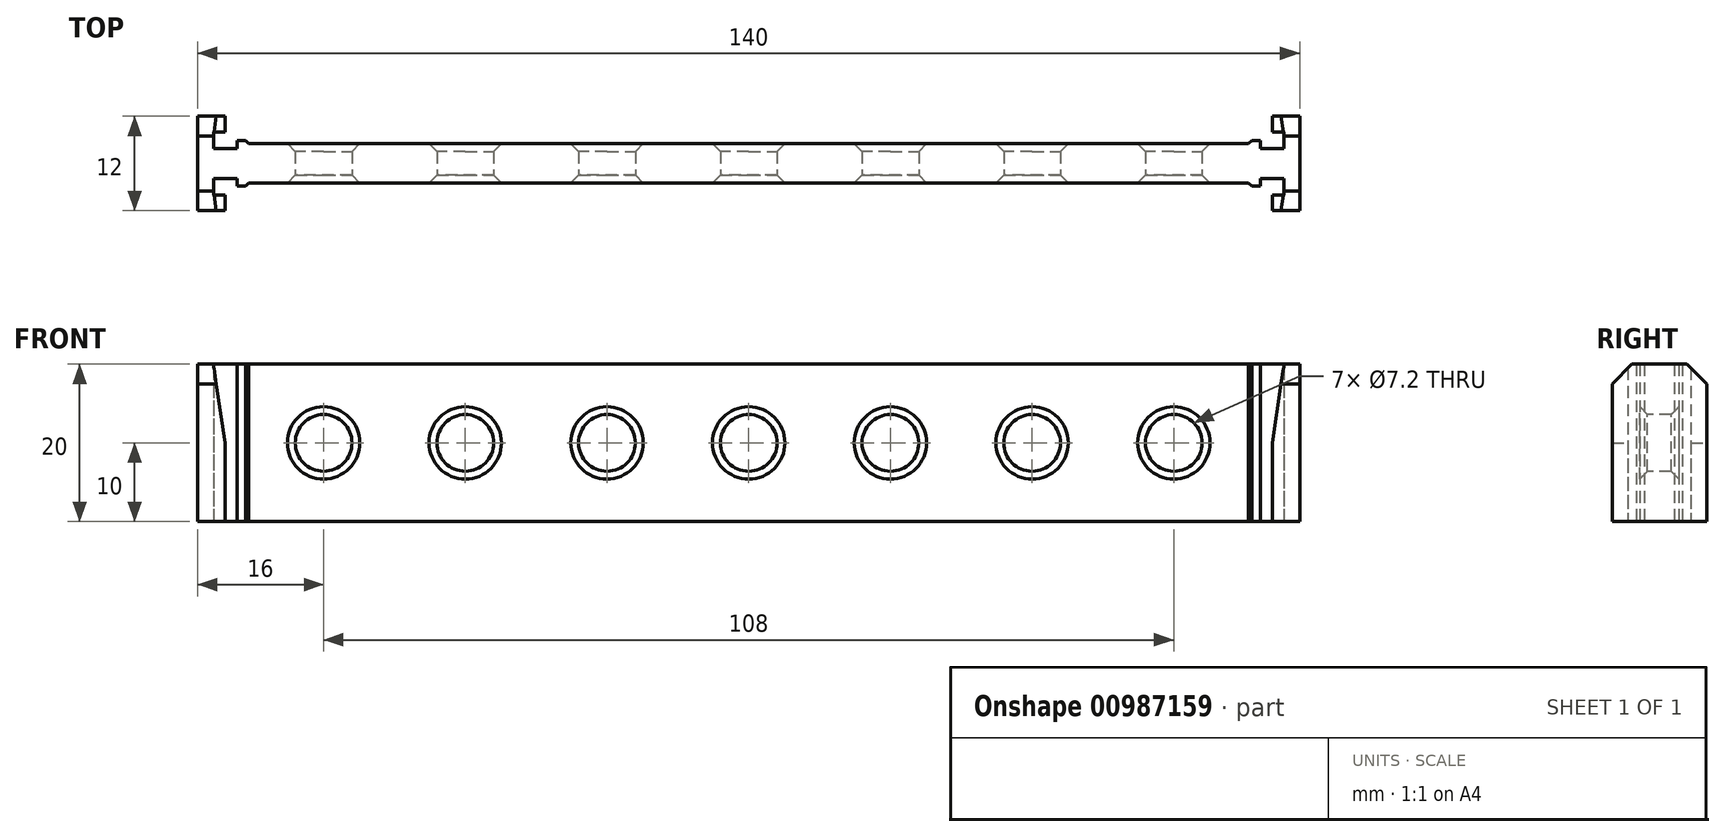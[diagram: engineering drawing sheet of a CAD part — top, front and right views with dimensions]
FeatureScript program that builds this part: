
annotation { "Feature Type Name" : "Feature", "Feature Type Description" : "" }
export const myFeature = defineFeature(function(context is Context, id is Id, definition is map)
    precondition{}
    {
        {
            var Q0;
            Q0=qCreatedBy(makeId("Top.planeOp"),FACE);
            var sketch = newSketch(context, id + "F0", { "sketchPlane" : qUnion([Q0])});
            skLineSegment(sketch, "E0", {"start": v(-70, 0) * mm, "end": v(-70, 6) * mm});
            skLineSegment(sketch, "E1", {"start": v(-70, 6) * mm, "end": v(-66.5, 6) * mm});
            skLineSegment(sketch, "E2", {"start": v(-66.5, 6) * mm, "end": v(-66.5, 4) * mm});
            skLineSegment(sketch, "E3", {"start": v(-66.5, 4) * mm, "end": v(-68, 4) * mm});
            skLineSegment(sketch, "E4", {"start": v(-68, 4) * mm, "end": v(-68, 1.9) * mm});
            skLineSegment(sketch, "E5", {"start": v(-68, 1.9) * mm, "end": v(-65, 1.9) * mm});
            skLineSegment(sketch, "E6", {"start": v(-65, 1.9) * mm, "end": v(-65, 2.9) * mm});
            skLineSegment(sketch, "E7", {"start": v(0, 2.5) * mm, "end": v(0, 0) * mm, "construction": true});
            skLineSegment(sketch, "E8", {"start": v(0, 0) * mm, "end": v(-70, 0) * mm, "construction": true});
            skLineSegment(sketch, "E9", {"start": v(0, 2.5) * mm, "end": v(-64, 2.5) * mm});
            skLineSegment(sketch, "E10", {"start": v(-65, 2.9) * mm, "end": v(-64, 2.9) * mm});
            skLineSegment(sketch, "E11", {"start": v(-64, 2.9) * mm, "end": v(-64, 2.5) * mm});
            skLineSegment(sketch, "E12.MirrorCS", {"start": v(-65, -2.9) * mm, "end": v(-64, -2.9) * mm});
            skLineSegment(sketch, "E13.MirrorCS", {"start": v(-64, -2.9) * mm, "end": v(-64, -2.5) * mm});
            skLineSegment(sketch, "E14.MirrorCS", {"start": v(-65, -1.9) * mm, "end": v(-65, -2.9) * mm});
            skLineSegment(sketch, "E15.MirrorCS", {"start": v(-66.5, -4) * mm, "end": v(-68, -4) * mm});
            skLineSegment(sketch, "E16.MirrorCS", {"start": v(-68, -1.9) * mm, "end": v(-65, -1.9) * mm});
            skLineSegment(sketch, "E17.MirrorCS", {"start": v(-66.5, -6) * mm, "end": v(-66.5, -4) * mm});
            skLineSegment(sketch, "E18.MirrorCS", {"start": v(-68, -4) * mm, "end": v(-68, -1.9) * mm});
            skLineSegment(sketch, "E19.MirrorCS", {"start": v(0, -2.5) * mm, "end": v(-64, -2.5) * mm});
            skLineSegment(sketch, "E20.MirrorCS", {"start": v(-70, -6) * mm, "end": v(-66.5, -6) * mm});
            skLineSegment(sketch, "E21.MirrorCS", {"start": v(-70, 0) * mm, "end": v(-70, -6) * mm});
            skLineSegment(sketch, "E22.MirrorCS", {"start": v(65, -2.9) * mm, "end": v(64, -2.9) * mm});
            skLineSegment(sketch, "E23.MirrorCS", {"start": v(64, 2.9) * mm, "end": v(64, 2.5) * mm});
            skLineSegment(sketch, "E24.MirrorCS", {"start": v(65, -1.9) * mm, "end": v(65, -2.9) * mm});
            skLineSegment(sketch, "E25.MirrorCS", {"start": v(65, 2.9) * mm, "end": v(64, 2.9) * mm});
            skLineSegment(sketch, "E26.MirrorCS", {"start": v(64, -2.9) * mm, "end": v(64, -2.5) * mm});
            skLineSegment(sketch, "E27.MirrorCS", {"start": v(65, 1.9) * mm, "end": v(65, 2.9) * mm});
            skLineSegment(sketch, "E28.MirrorCS", {"start": v(66.5, 4) * mm, "end": v(68, 4) * mm});
            skLineSegment(sketch, "E29.MirrorCS", {"start": v(68, 1.9) * mm, "end": v(65, 1.9) * mm});
            skLineSegment(sketch, "E30.MirrorCS", {"start": v(68, -1.9) * mm, "end": v(65, -1.9) * mm});
            skLineSegment(sketch, "E31.MirrorCS", {"start": v(68, 4) * mm, "end": v(68, 1.9) * mm});
            skLineSegment(sketch, "E32.MirrorCS", {"start": v(0, 2.5) * mm, "end": v(64, 2.5) * mm});
            skLineSegment(sketch, "E33.MirrorCS", {"start": v(0, -2.5) * mm, "end": v(64, -2.5) * mm});
            skLineSegment(sketch, "E34.MirrorCS", {"start": v(66.5, -4) * mm, "end": v(68, -4) * mm});
            skLineSegment(sketch, "E35.MirrorCS", {"start": v(70, -6) * mm, "end": v(66.5, -6) * mm});
            skLineSegment(sketch, "E36.MirrorCS", {"start": v(66.5, -6) * mm, "end": v(66.5, -4) * mm});
            skLineSegment(sketch, "E37.MirrorCS", {"start": v(70, 0) * mm, "end": v(70, 6) * mm});
            skLineSegment(sketch, "E38.MirrorCS", {"start": v(66.5, 6) * mm, "end": v(66.5, 4) * mm});
            skLineSegment(sketch, "E39.MirrorCS", {"start": v(70, 0) * mm, "end": v(70, -6) * mm});
            skLineSegment(sketch, "E40.MirrorCS", {"start": v(68, -4) * mm, "end": v(68, -1.9) * mm});
            skLineSegment(sketch, "E41.MirrorCS", {"start": v(70, 6) * mm, "end": v(66.5, 6) * mm});
            skSolve(sketch);
        }
        {
            var Q0;
            Q0=makeQuery(id+"F0.imprint","IMPRINT",FACE,{"disambiguationData":[TD([[makeQuery(id+"F0.imprint","IMPRINT",EDGE,{"derivedFrom":sQuery(id+"F0.wireOp",EDGE,"E0")}),-1.0]])]});
            extrude(context, id + "F1", {"entities" : qUnion([Q0]), "depth" : 20 * mm, "offsetDistance" : 25 * mm});
        }
        {
            var Q0;
            Q0=makeQuery(id+"F1.opExtrude","SWEPT_EDGE",EDGE,{"disambiguationData":[OSD([sQuery(id+"F0.wireOp",EDGE,"E9"),sQuery(id+"F0.wireOp",EDGE,"E11")])]});
            var Q1;
            Q1=makeQuery(id+"F1.opExtrude","SWEPT_EDGE",EDGE,{"disambiguationData":[OSD([sQuery(id+"F0.wireOp",EDGE,"E13.MirrorCS"),sQuery(id+"F0.wireOp",EDGE,"E19.MirrorCS")])]});
            var Q2;
            Q2=makeQuery(id+"F1.opExtrude","SWEPT_EDGE",EDGE,{"disambiguationData":[OSD([sQuery(id+"F0.wireOp",EDGE,"E26.MirrorCS"),sQuery(id+"F0.wireOp",EDGE,"E33.MirrorCS")])]});
            var Q3;
            Q3=makeQuery(id+"F1.opExtrude","SWEPT_EDGE",EDGE,{"disambiguationData":[OSD([sQuery(id+"F0.wireOp",EDGE,"E23.MirrorCS"),sQuery(id+"F0.wireOp",EDGE,"E32.MirrorCS")])]});
            chamfer(context, id + "F2", {"entities" : qUnion([Q0, Q1, Q2, Q3]), "width" : 0.5 * mm, "tangentPropagation" : true});
        }
        {
            var Q0;
            Q0=makeQuery(id+"F1.opExtrude","CAP_EDGE",EDGE,{"disambiguationData":[OSD([sQuery(id+"F0.wireOp",EDGE,"E2")])],"isStart":false});
            var Q1;
            Q1=makeQuery(id+"F1.opExtrude","CAP_EDGE",EDGE,{"disambiguationData":[OSD([sQuery(id+"F0.wireOp",EDGE,"E17.MirrorCS")])],"isStart":false});
            var Q2;
            Q2=makeQuery(id+"F1.opExtrude","CAP_EDGE",EDGE,{"disambiguationData":[OSD([sQuery(id+"F0.wireOp",EDGE,"E38.MirrorCS")])],"isStart":false});
            var Q3;
            Q3=makeQuery(id+"F1.opExtrude","CAP_EDGE",EDGE,{"disambiguationData":[OSD([sQuery(id+"F0.wireOp",EDGE,"E36.MirrorCS")])],"isStart":false});
            chamfer(context, id + "F3", {"entities" : qUnion([Q0, Q1, Q2, Q3]), "chamferType" : ChamferType.TWO_OFFSETS, "width1" : 10 * mm, "oppositeDirection" : false, "width2" : 1.5 * mm, "tangentPropagation" : true});
        }
        {
            var Q0;
            Q0=makeQuery(id+"F1.opExtrude","CAP_EDGE",EDGE,{"disambiguationData":[OSD([sQuery(id+"F0.wireOp",EDGE,"E1")])],"isStart":false});
            var Q1;
            Q1=makeQuery(id+"F1.opExtrude","CAP_EDGE",EDGE,{"disambiguationData":[OSD([sQuery(id+"F0.wireOp",EDGE,"E20.MirrorCS")])],"isStart":false});
            var Q2;
            Q2=makeQuery(id+"F1.opExtrude","CAP_EDGE",EDGE,{"disambiguationData":[OSD([sQuery(id+"F0.wireOp",EDGE,"E41.MirrorCS")])],"isStart":false});
            var Q3;
            Q3=makeQuery(id+"F1.opExtrude","CAP_EDGE",EDGE,{"disambiguationData":[OSD([sQuery(id+"F0.wireOp",EDGE,"E35.MirrorCS")])],"isStart":false});
            chamfer(context, id + "F4", {"entities" : qUnion([Q0, Q1, Q2, Q3]), "width" : 2.5 * mm, "tangentPropagation" : true});
        }
        {
            var Q0;
            Q0=makeQuery(id+"F1.opExtrude","SWEPT_FACE",FACE,{"disambiguationData":[OSD([sQuery(id+"F0.wireOp",EDGE,"E19.MirrorCS"),sQuery(id+"F0.wireOp",EDGE,"E33.MirrorCS")])]});
            var sketch = newSketch(context, id + "F5", { "sketchPlane" : qUnion([Q0])});
            skCircle(sketch, "E42", {"center": v(-54, 10) * mm, "radius": 3.6 * mm});
            skCircle(sketch, "E43.1.0.0", {"center": v(-36, 10) * mm, "radius": 3.6 * mm});
            skCircle(sketch, "E43.2.0.0", {"center": v(-18, 10) * mm, "radius": 3.6 * mm});
            skCircle(sketch, "E43.3.0.0", {"center": v(0, 10) * mm, "radius": 3.6 * mm});
            skCircle(sketch, "E43.4.0.0", {"center": v(18, 10) * mm, "radius": 3.6 * mm});
            skCircle(sketch, "E43.5.0.0", {"center": v(36, 10) * mm, "radius": 3.6 * mm});
            skCircle(sketch, "E43.6.0.0", {"center": v(54, 10) * mm, "radius": 3.6 * mm});
            skLineSegment(sketch, "E43.direction1", {"start": v(-54, 10) * mm, "end": v(-36, 10) * mm, "construction": true});
            skSolve(sketch);
        }
        {
            var Q0;
            Q0 = qSketchRegion(id + "F5", true);
            extrude(context, id + "F6", {"entities" : qUnion([Q0]), "operationType" : NewBodyOperationType.REMOVE, "oppositeDirection" : true, "depth" : 25 * mm, "offsetDistance" : 25 * mm});
        }
        {
            var Q0;
            Q0=makeQuery(id+"F6.boolean.opBoolean","COPY",FACE,{"derivedFrom":makeQuery(id+"F6.opExtrude","SWEPT_FACE",FACE,{"disambiguationData":[OSD([sQuery(id+"F5.wireOp",EDGE,"E42")])]})});
            var Q1;
            Q1=makeQuery(id+"F6.boolean.opBoolean","COPY",FACE,{"derivedFrom":makeQuery(id+"F6.opExtrude","SWEPT_FACE",FACE,{"disambiguationData":[OSD([sQuery(id+"F5.wireOp",EDGE,"E43.1.0.0")])]})});
            var Q2;
            Q2=makeQuery(id+"F6.boolean.opBoolean","COPY",FACE,{"derivedFrom":makeQuery(id+"F6.opExtrude","SWEPT_FACE",FACE,{"disambiguationData":[OSD([sQuery(id+"F5.wireOp",EDGE,"E43.2.0.0")])]})});
            var Q3;
            Q3=makeQuery(id+"F6.boolean.opBoolean","COPY",FACE,{"derivedFrom":makeQuery(id+"F6.opExtrude","SWEPT_FACE",FACE,{"disambiguationData":[OSD([sQuery(id+"F5.wireOp",EDGE,"E43.3.0.0")])]})});
            var Q4;
            Q4=makeQuery(id+"F6.boolean.opBoolean","COPY",FACE,{"derivedFrom":makeQuery(id+"F6.opExtrude","SWEPT_FACE",FACE,{"disambiguationData":[OSD([sQuery(id+"F5.wireOp",EDGE,"E43.4.0.0")])]})});
            var Q5;
            Q5=makeQuery(id+"F6.boolean.opBoolean","COPY",FACE,{"derivedFrom":makeQuery(id+"F6.opExtrude","SWEPT_FACE",FACE,{"disambiguationData":[OSD([sQuery(id+"F5.wireOp",EDGE,"E43.5.0.0")])]})});
            var Q6;
            Q6=makeQuery(id+"F6.boolean.opBoolean","COPY",FACE,{"derivedFrom":makeQuery(id+"F6.opExtrude","SWEPT_FACE",FACE,{"disambiguationData":[OSD([sQuery(id+"F5.wireOp",EDGE,"E43.6.0.0")])]})});
            chamfer(context, id + "F7", {"entities" : qUnion([Q0, Q1, Q2, Q3, Q4, Q5, Q6]), "width" : 1 * mm, "tangentPropagation" : true});
        }
    });
